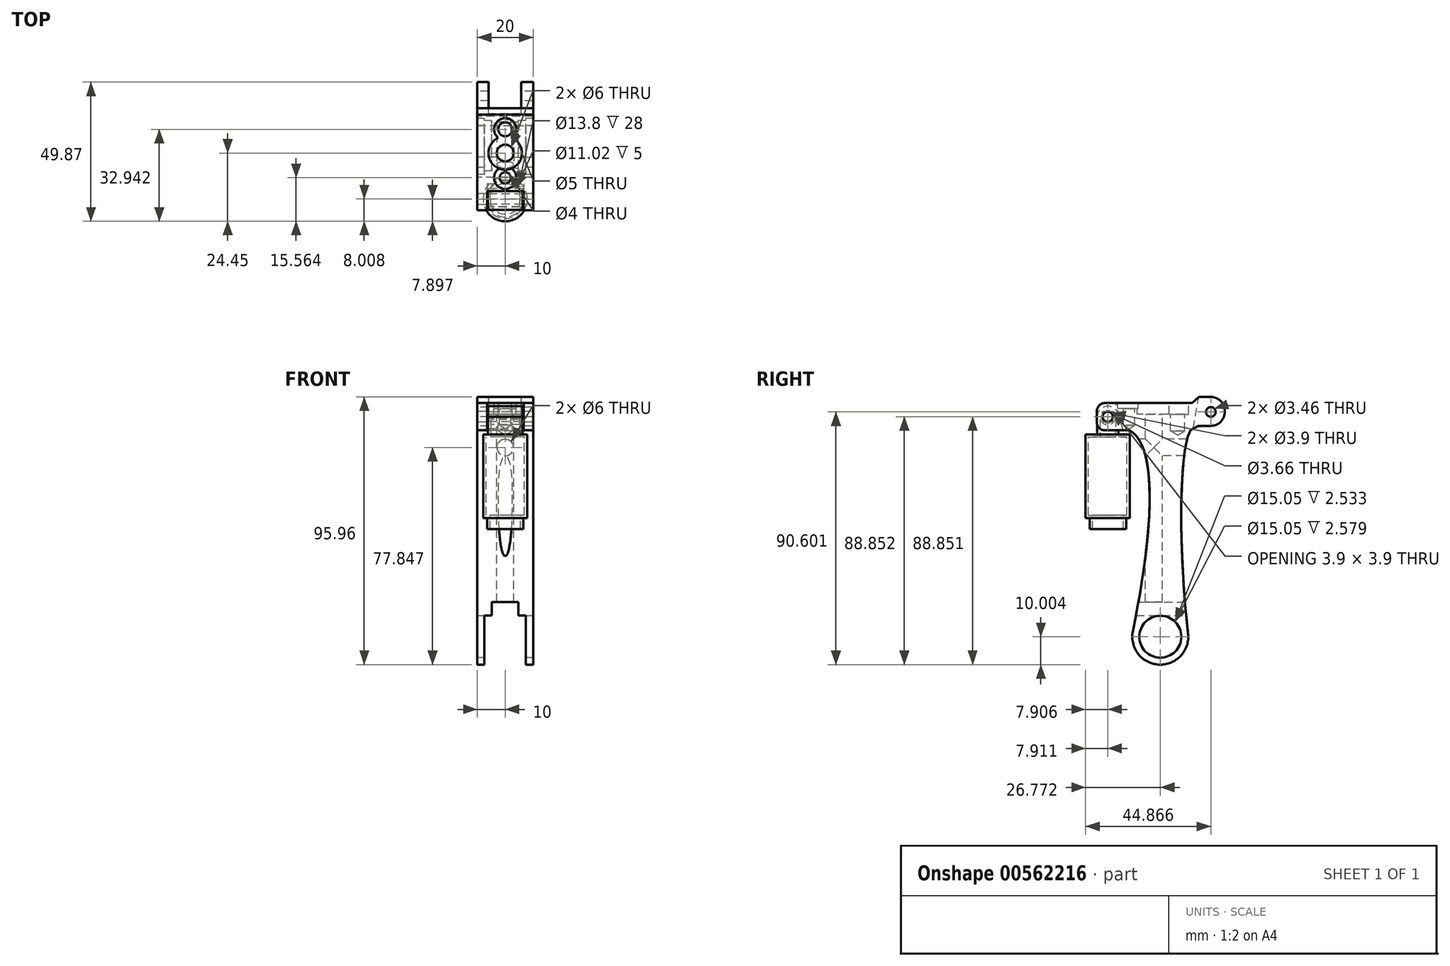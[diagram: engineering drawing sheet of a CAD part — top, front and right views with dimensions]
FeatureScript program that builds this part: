
annotation { "Feature Type Name" : "Feature", "Feature Type Description" : "" }
export const myFeature = defineFeature(function(context is Context, id is Id, definition is map)
    precondition{}
    {
        {
            var Q0;
            Q0=qCreatedBy(makeId("Right.planeOp"),FACE);
            var sketch = newSketch(context, id + "F0", { "sketchPlane" : qUnion([Q0])});
            skLineSegment(sketch, "E0", {"start": v(-11.53, -4.6) * mm, "end": v(-15.88, -4.6) * mm});
            skLineSegment(sketch, "E1", {"start": v(-15.88, -4.6) * mm, "end": v(-18.18, -6.8) * mm});
            skLineSegment(sketch, "E2", {"start": v(-18.18, -6.8) * mm, "end": v(-49.43, -6.8) * mm});
            skLineSegment(sketch, "E3", {"start": v(-52.43, -9.8) * mm, "end": v(-52.43, -13.6) * mm});
            skLineSegment(sketch, "E4", {"start": v(-49.43, -16.6) * mm, "end": v(-40.63, -16.6) * mm});
            skLineSegment(sketch, "E5", {"start": v(-6.53, -9.6) * mm, "end": v(-6.53, -9.97) * mm});
            skLineSegment(sketch, "E6", {"start": v(-11.53, -14.97) * mm, "end": v(-16.03, -14.97) * mm});
            skLineSegment(sketch, "E7", {"start": v(-16.03, -14.97) * mm, "end": v(-18.84, -16.6) * mm});
            skFitSpline(sketch, "E8", {"points": [v(-18.84, -16.6) * mm, v(-18.36, -99.99) * mm], "startDerivative": vector(-12.08, -19.93) * mm, "endDerivative": vector(16.3, -116.19) * mm});
            skFitSpline(sketch, "E9", {"points": [v(-40.63, -16.6) * mm, v(-42.25, -101.24) * mm], "startDerivative": vector(34.93, -19.93) * mm, "endDerivative": vector(-27.8, -119.95) * mm});
            skArc(sketch, "E10.filletArc", {"start": v(-6.53, -9.6) * mm, "mid": v(-8, -6.07) * mm, "end": v(-11.53, -4.6) * mm});
            skArc(sketch, "E11.filletArc", {"start": v(-11.53, -14.97) * mm, "mid": v(-8, -13.5) * mm, "end": v(-6.53, -9.97) * mm});
            skArc(sketch, "E12.filletArc", {"start": v(-49.43, -6.8) * mm, "mid": v(-51.55, -7.67) * mm, "end": v(-52.43, -9.8) * mm});
            skPoint(sketch, "E13.center.orphan", {"position": v(-30.3, -100.61) * mm});
            skLineSegment(sketch, "E14", {"start": v(-29.1, -100.55) * mm, "end": v(-29.16, -100.55) * mm});
            skArc(sketch, "E15.filletArc", {"start": v(-29.1, -100.55) * mm, "mid": v(-22, -97.03) * mm, "end": v(-19.7, -89.45) * mm});
            skArc(sketch, "E16.filletArc", {"start": v(-39.48, -88.56) * mm, "mid": v(-37.26, -97.1) * mm, "end": v(-29.16, -100.55) * mm});
            skArc(sketch, "E17.filletArc", {"start": v(-52.43, -13.6) * mm, "mid": v(-51.55, -15.72) * mm, "end": v(-49.43, -16.6) * mm});
            skCircle(sketch, "E18", {"center": v(-29.63, -90.57) * mm, "radius": 7.53 * mm});
            skCircle(sketch, "E19", {"center": v(-48.5, -11.72) * mm, "radius": 1.95 * mm});
            skCircle(sketch, "E20", {"center": v(-11.53, -9.97) * mm, "radius": 1.73 * mm});
            skSolve(sketch);
        }
        {
            var Q0;
            Q0 = qSketchRegion(id + "F0", true);
            extrude(context, id + "F1", {"entities" : qUnion([Q0]), "endBound" : BoundingType.SYMMETRIC, "depth" : 20 * mm, "offsetDistance" : 25 * mm});
        }
        {
            var Q0;
            Q0=makeQuery(id+"F1.opExtrude","SWEPT_FACE",FACE,{"disambiguationData":[OSD([sQuery(id+"F0.wireOp",EDGE,"E2")])]});
            var sketch = newSketch(context, id + "F2", { "sketchPlane" : qUnion([Q0])});
            skPoint(sketch, "E21", {"position": v(0, -31.95) * mm});
            skPoint(sketch, "E22", {"position": v(0, -23.46) * mm});
            skPoint(sketch, "E22.positionSnap0", {"position": v(0, -18.18) * mm});
            skPoint(sketch, "E23", {"position": v(0, -40.84) * mm});
            skSolve(sketch);
        }
        {
            var Q0;
            Q0=sQuery(id+"F2.wireOp",VERTEX,"E21");
            var Q1;
            Q1=makeQuery(id+"F1.opExtrude","SWEPT_BODY",BODY,{"disambiguationData":[OSD([sQuery(id+"F0.wireOp",EDGE,"E0"),sQuery(id+"F0.wireOp",EDGE,"E1"),sQuery(id+"F0.wireOp",EDGE,"E2"),sQuery(id+"F0.wireOp",EDGE,"E3"),sQuery(id+"F0.wireOp",EDGE,"E4"),sQuery(id+"F0.wireOp",EDGE,"E5"),sQuery(id+"F0.wireOp",EDGE,"E6"),sQuery(id+"F0.wireOp",EDGE,"E7"),sQuery(id+"F0.wireOp",EDGE,"E8"),sQuery(id+"F0.wireOp",EDGE,"E9"),sQuery(id+"F0.wireOp",EDGE,"E10.filletArc"),sQuery(id+"F0.wireOp",EDGE,"E11.filletArc"),sQuery(id+"F0.wireOp",EDGE,"E12.filletArc"),sQuery(id+"F0.wireOp",EDGE,"E14"),sQuery(id+"F0.wireOp",EDGE,"E15.filletArc"),sQuery(id+"F0.wireOp",EDGE,"E16.filletArc"),sQuery(id+"F0.wireOp",EDGE,"E17.filletArc"),sQuery(id+"F0.wireOp",EDGE,"E18"),sQuery(id+"F0.wireOp",EDGE,"E19"),sQuery(id+"F0.wireOp",EDGE,"E20")])]});
            hole(context, id + "F3", {"style" : HoleStyle.C_BORE, "endStyle" : HoleEndStyle.BLIND, "holeDiameter" : 6 * mm, "cBoreDiameter" : 12 * mm, "cBoreDepth" : 4 * mm, "majorDiameter" : 5 * mm, "holeDepth" : 80 * mm, "isTappedThrough" : true, "tappedDepth" : 12 * mm, "tapClearance" : 3, "startFromSketch" : true, "locations" : qUnion([Q0]), "scope" : qUnion([Q1])});
        }
        {
            var Q0;
            Q0=sQuery(id+"F2.wireOp",VERTEX,"E22");
            var Q1;
            Q1=makeQuery(id+"F1.opExtrude","SWEPT_BODY",BODY,{"disambiguationData":[OSD([sQuery(id+"F0.wireOp",EDGE,"E0"),sQuery(id+"F0.wireOp",EDGE,"E1"),sQuery(id+"F0.wireOp",EDGE,"E2"),sQuery(id+"F0.wireOp",EDGE,"E3"),sQuery(id+"F0.wireOp",EDGE,"E4"),sQuery(id+"F0.wireOp",EDGE,"E5"),sQuery(id+"F0.wireOp",EDGE,"E6"),sQuery(id+"F0.wireOp",EDGE,"E7"),sQuery(id+"F0.wireOp",EDGE,"E8"),sQuery(id+"F0.wireOp",EDGE,"E9"),sQuery(id+"F0.wireOp",EDGE,"E10.filletArc"),sQuery(id+"F0.wireOp",EDGE,"E11.filletArc"),sQuery(id+"F0.wireOp",EDGE,"E12.filletArc"),sQuery(id+"F0.wireOp",EDGE,"E14"),sQuery(id+"F0.wireOp",EDGE,"E15.filletArc"),sQuery(id+"F0.wireOp",EDGE,"E16.filletArc"),sQuery(id+"F0.wireOp",EDGE,"E17.filletArc"),sQuery(id+"F0.wireOp",EDGE,"E18"),sQuery(id+"F0.wireOp",EDGE,"E19"),sQuery(id+"F0.wireOp",EDGE,"E20")])]});
            hole(context, id + "F4", {"style" : HoleStyle.C_BORE, "endStyle" : HoleEndStyle.BLIND, "holeDiameter" : 5 * mm, "cBoreDiameter" : 8 * mm, "cBoreDepth" : 4 * mm, "majorDiameter" : 5 * mm, "holeDepth" : 10 * mm, "isTappedThrough" : true, "tappedDepth" : 12 * mm, "tapClearance" : 3, "startFromSketch" : true, "locations" : qUnion([Q0]), "scope" : qUnion([Q1])});
        }
        {
            var Q0;
            Q0=sQuery(id+"F2.wireOp",VERTEX,"E23");
            var Q1;
            Q1=makeQuery(id+"F1.opExtrude","SWEPT_BODY",BODY,{"disambiguationData":[OSD([sQuery(id+"F0.wireOp",EDGE,"E0"),sQuery(id+"F0.wireOp",EDGE,"E1"),sQuery(id+"F0.wireOp",EDGE,"E2"),sQuery(id+"F0.wireOp",EDGE,"E3"),sQuery(id+"F0.wireOp",EDGE,"E4"),sQuery(id+"F0.wireOp",EDGE,"E5"),sQuery(id+"F0.wireOp",EDGE,"E6"),sQuery(id+"F0.wireOp",EDGE,"E7"),sQuery(id+"F0.wireOp",EDGE,"E8"),sQuery(id+"F0.wireOp",EDGE,"E9"),sQuery(id+"F0.wireOp",EDGE,"E10.filletArc"),sQuery(id+"F0.wireOp",EDGE,"E11.filletArc"),sQuery(id+"F0.wireOp",EDGE,"E12.filletArc"),sQuery(id+"F0.wireOp",EDGE,"E14"),sQuery(id+"F0.wireOp",EDGE,"E15.filletArc"),sQuery(id+"F0.wireOp",EDGE,"E16.filletArc"),sQuery(id+"F0.wireOp",EDGE,"E17.filletArc"),sQuery(id+"F0.wireOp",EDGE,"E18"),sQuery(id+"F0.wireOp",EDGE,"E19"),sQuery(id+"F0.wireOp",EDGE,"E20")])]});
            hole(context, id + "F5", {"style" : HoleStyle.C_BORE, "endStyle" : HoleEndStyle.BLIND, "holeDiameter" : 4 * mm, "cBoreDiameter" : 8 * mm, "cBoreDepth" : 2 * mm, "majorDiameter" : 5 * mm, "holeDepth" : 8 * mm, "isTappedThrough" : true, "tappedDepth" : 12 * mm, "tapClearance" : 3, "startFromSketch" : true, "locations" : qUnion([Q0]), "scope" : qUnion([Q1])});
        }
        {
            var Q0;
            Q0=makeQuery(id+"F1.opExtrude","SWEPT_FACE",FACE,{"disambiguationData":[OSD([sQuery(id+"F0.wireOp",EDGE,"E3")])]});
            var sketch = newSketch(context, id + "F6", { "sketchPlane" : qUnion([Q0])});
            skPoint(sketch, "E24", {"position": v(0, -22.72) * mm});
            skPoint(sketch, "E25", {"position": v(0, -71.93) * mm});
            skSolve(sketch);
        }
        {
            var Q0;
            Q0=sQuery(id+"F6.wireOp",VERTEX,"E24");
            var Q1;
            Q1=makeQuery(id+"F1.opExtrude","SWEPT_BODY",BODY,{"disambiguationData":[OSD([sQuery(id+"F0.wireOp",EDGE,"E0"),sQuery(id+"F0.wireOp",EDGE,"E1"),sQuery(id+"F0.wireOp",EDGE,"E2"),sQuery(id+"F0.wireOp",EDGE,"E3"),sQuery(id+"F0.wireOp",EDGE,"E4"),sQuery(id+"F0.wireOp",EDGE,"E5"),sQuery(id+"F0.wireOp",EDGE,"E6"),sQuery(id+"F0.wireOp",EDGE,"E7"),sQuery(id+"F0.wireOp",EDGE,"E8"),sQuery(id+"F0.wireOp",EDGE,"E9"),sQuery(id+"F0.wireOp",EDGE,"E10.filletArc"),sQuery(id+"F0.wireOp",EDGE,"E11.filletArc"),sQuery(id+"F0.wireOp",EDGE,"E12.filletArc"),sQuery(id+"F0.wireOp",EDGE,"E14"),sQuery(id+"F0.wireOp",EDGE,"E15.filletArc"),sQuery(id+"F0.wireOp",EDGE,"E16.filletArc"),sQuery(id+"F0.wireOp",EDGE,"E17.filletArc"),sQuery(id+"F0.wireOp",EDGE,"E18"),sQuery(id+"F0.wireOp",EDGE,"E19"),sQuery(id+"F0.wireOp",EDGE,"E20")])]});
            hole(context, id + "F7", {"style" : HoleStyle.SIMPLE, "endStyle" : HoleEndStyle.BLIND, "holeDiameter" : 6 * mm, "majorDiameter" : 5 * mm, "holeDepth" : 40 * mm, "isTappedThrough" : true, "tappedDepth" : 12 * mm, "tapClearance" : 3, "startFromSketch" : true, "locations" : qUnion([Q0]), "scope" : qUnion([Q1])});
        }
        {
            var Q0;
            Q0=qCreatedBy(makeId("Front.planeOp"),FACE);
            var sketch = newSketch(context, id + "F8", { "sketchPlane" : qUnion([Q0])});
            skLineSegment(sketch, "E26.bottom", {"start": v(-7.47, -82.93) * mm, "end": v(7.42, -82.93) * mm});
            skLineSegment(sketch, "E26.top", {"start": v(-7.47, -100.7) * mm, "end": v(7.42, -100.7) * mm});
            skLineSegment(sketch, "E26.left", {"start": v(-7.47, -82.93) * mm, "end": v(-7.47, -100.7) * mm});
            skLineSegment(sketch, "E26.right", {"start": v(7.42, -82.93) * mm, "end": v(7.42, -100.7) * mm});
            skSolve(sketch);
        }
        {
            var Q0;
            Q0=makeQuery(id+"F8.imprint","IMPRINT",FACE,{"disambiguationData":[TD([[makeQuery(id+"F8.imprint","IMPRINT",EDGE,{"derivedFrom":sQuery(id+"F8.wireOp",EDGE,"E26.bottom")}),-1.0]])]});
            extrude(context, id + "F9", {"entities" : qUnion([Q0]), "endBound" : BoundingType.THROUGH_ALL, "depth" : 25 * mm, "offsetDistance" : 25 * mm});
        }
        {
            var Q0;
            Q0=makeQuery(id+"F9.opExtrude","SWEPT_BODY",BODY,{"disambiguationData":[OSD([sQuery(id+"F8.wireOp",EDGE,"E26.bottom"),sQuery(id+"F8.wireOp",EDGE,"E26.top"),sQuery(id+"F8.wireOp",EDGE,"E26.left"),sQuery(id+"F8.wireOp",EDGE,"E26.right")])]});
            var Q1;
            Q1=makeQuery(id+"F1.opExtrude","SWEPT_BODY",BODY,{"disambiguationData":[OSD([sQuery(id+"F0.wireOp",EDGE,"E0"),sQuery(id+"F0.wireOp",EDGE,"E1"),sQuery(id+"F0.wireOp",EDGE,"E2"),sQuery(id+"F0.wireOp",EDGE,"E3"),sQuery(id+"F0.wireOp",EDGE,"E4"),sQuery(id+"F0.wireOp",EDGE,"E5"),sQuery(id+"F0.wireOp",EDGE,"E6"),sQuery(id+"F0.wireOp",EDGE,"E7"),sQuery(id+"F0.wireOp",EDGE,"E8"),sQuery(id+"F0.wireOp",EDGE,"E9"),sQuery(id+"F0.wireOp",EDGE,"E10.filletArc"),sQuery(id+"F0.wireOp",EDGE,"E11.filletArc"),sQuery(id+"F0.wireOp",EDGE,"E12.filletArc"),sQuery(id+"F0.wireOp",EDGE,"E14"),sQuery(id+"F0.wireOp",EDGE,"E15.filletArc"),sQuery(id+"F0.wireOp",EDGE,"E16.filletArc"),sQuery(id+"F0.wireOp",EDGE,"E17.filletArc"),sQuery(id+"F0.wireOp",EDGE,"E18"),sQuery(id+"F0.wireOp",EDGE,"E19"),sQuery(id+"F0.wireOp",EDGE,"E20")])]});
            booleanBodies(context, id + "F10", {"operationType" : BooleanOperationType.SUBTRACTION, "tools" : qUnion([Q0]), "targets" : qUnion([Q1])});
        }
        {
            var Q0;
            Q0=qCreatedBy(makeId("Top.planeOp"),FACE);
            var sketch = newSketch(context, id + "F11", { "sketchPlane" : qUnion([Q0])});
            skLineSegment(sketch, "E27.bottom", {"start": v(-6.5, -47.75) * mm, "end": v(6.55, -47.75) * mm});
            skLineSegment(sketch, "E27.top", {"start": v(-6.5, -57.6) * mm, "end": v(6.55, -57.6) * mm});
            skLineSegment(sketch, "E27.left", {"start": v(-6.5, -47.75) * mm, "end": v(-6.5, -57.6) * mm});
            skLineSegment(sketch, "E27.right", {"start": v(6.55, -47.75) * mm, "end": v(6.55, -57.6) * mm});
            skSolve(sketch);
        }
        {
            var Q0;
            Q0 = qSketchRegion(id + "F11", true);
            extrude(context, id + "F12", {"entities" : qUnion([Q0]), "oppositeDirection" : true, "depth" : 25 * mm, "offsetDistance" : 25 * mm});
        }
        {
            var Q0;
            Q0=makeQuery(id+"F12.opExtrude","SWEPT_BODY",BODY,{"disambiguationData":[OSD([sQuery(id+"F11.wireOp",EDGE,"E27.bottom"),sQuery(id+"F11.wireOp",EDGE,"E27.top"),sQuery(id+"F11.wireOp",EDGE,"E27.left"),sQuery(id+"F11.wireOp",EDGE,"E27.right")])]});
            var Q1;
            Q1=makeQuery(id+"F12.opExtrude","CAP_EDGE",EDGE,{"disambiguationData":[OSD([sQuery(id+"F11.wireOp",EDGE,"E27.top")])],"isStart":true});
            transform(context, id + "F13", {"entities" : qUnion([Q0]), "transformType" : TransformType.ROTATION, "transformAxis" : qUnion([Q1]), "angle" : 15 * degree, "makeCopy" : false});
        }
        {
            var Q0;
            Q0=makeQuery(id+"F12.opExtrude","SWEPT_BODY",BODY,{"disambiguationData":[OSD([sQuery(id+"F11.wireOp",EDGE,"E27.bottom"),sQuery(id+"F11.wireOp",EDGE,"E27.top"),sQuery(id+"F11.wireOp",EDGE,"E27.left"),sQuery(id+"F11.wireOp",EDGE,"E27.right")])]});
            var Q1;
            Q1=makeQuery(id+"F1.opExtrude","SWEPT_BODY",BODY,{"disambiguationData":[OSD([sQuery(id+"F0.wireOp",EDGE,"E0"),sQuery(id+"F0.wireOp",EDGE,"E1"),sQuery(id+"F0.wireOp",EDGE,"E2"),sQuery(id+"F0.wireOp",EDGE,"E3"),sQuery(id+"F0.wireOp",EDGE,"E4"),sQuery(id+"F0.wireOp",EDGE,"E5"),sQuery(id+"F0.wireOp",EDGE,"E6"),sQuery(id+"F0.wireOp",EDGE,"E7"),sQuery(id+"F0.wireOp",EDGE,"E8"),sQuery(id+"F0.wireOp",EDGE,"E9"),sQuery(id+"F0.wireOp",EDGE,"E10.filletArc"),sQuery(id+"F0.wireOp",EDGE,"E11.filletArc"),sQuery(id+"F0.wireOp",EDGE,"E12.filletArc"),sQuery(id+"F0.wireOp",EDGE,"E14"),sQuery(id+"F0.wireOp",EDGE,"E15.filletArc"),sQuery(id+"F0.wireOp",EDGE,"E16.filletArc"),sQuery(id+"F0.wireOp",EDGE,"E17.filletArc"),sQuery(id+"F0.wireOp",EDGE,"E18"),sQuery(id+"F0.wireOp",EDGE,"E19"),sQuery(id+"F0.wireOp",EDGE,"E20")])]});
            booleanBodies(context, id + "F14", {"operationType" : BooleanOperationType.SUBTRACTION, "tools" : qUnion([Q0]), "targets" : qUnion([Q1])});
        }
        {
            var Q0;
            Q0=qCreatedBy(makeId("Top.planeOp"),FACE);
            var sketch = newSketch(context, id + "F15", { "sketchPlane" : qUnion([Q0])});
            skLineSegment(sketch, "E28.bottom", {"start": v(-4.83, -40.06) * mm, "end": v(4.68, -40.06) * mm});
            skLineSegment(sketch, "E28.top", {"start": v(-4.83, -19.56) * mm, "end": v(4.68, -19.56) * mm});
            skLineSegment(sketch, "E28.left", {"start": v(-4.83, -40.06) * mm, "end": v(-4.83, -19.56) * mm});
            skLineSegment(sketch, "E28.right", {"start": v(4.68, -40.06) * mm, "end": v(4.68, -19.56) * mm});
            skSolve(sketch);
        }
        {
            var Q0;
            Q0 = qSketchRegion(id + "F15", true);
            extrude(context, id + "F16", {"entities" : qUnion([Q0]), "oppositeDirection" : true, "depth" : 10 * mm, "offsetDistance" : 25 * mm});
        }
        {
            var Q0;
            Q0=makeQuery(id+"F16.opExtrude","SWEPT_BODY",BODY,{"disambiguationData":[OSD([sQuery(id+"F15.wireOp",EDGE,"E28.bottom"),sQuery(id+"F15.wireOp",EDGE,"E28.top"),sQuery(id+"F15.wireOp",EDGE,"E28.left"),sQuery(id+"F15.wireOp",EDGE,"E28.right")])]});
            transform(context, id + "F17", {"entities" : qUnion([Q0]), "transformType" : TransformType.TRANSLATION_3D, "dx" : 0 * mm, "dy" : 1.5 * mm, "dz" : -78.1 * mm, "makeCopy" : false});
        }
        {
            var Q0;
            Q0=makeQuery(id+"F16.opExtrude","SWEPT_BODY",BODY,{"disambiguationData":[OSD([sQuery(id+"F15.wireOp",EDGE,"E28.bottom"),sQuery(id+"F15.wireOp",EDGE,"E28.top"),sQuery(id+"F15.wireOp",EDGE,"E28.left"),sQuery(id+"F15.wireOp",EDGE,"E28.right")])]});
            var Q1;
            Q1=makeQuery(id+"F1.opExtrude","SWEPT_BODY",BODY,{"disambiguationData":[OSD([sQuery(id+"F0.wireOp",EDGE,"E0"),sQuery(id+"F0.wireOp",EDGE,"E1"),sQuery(id+"F0.wireOp",EDGE,"E2"),sQuery(id+"F0.wireOp",EDGE,"E3"),sQuery(id+"F0.wireOp",EDGE,"E4"),sQuery(id+"F0.wireOp",EDGE,"E5"),sQuery(id+"F0.wireOp",EDGE,"E6"),sQuery(id+"F0.wireOp",EDGE,"E7"),sQuery(id+"F0.wireOp",EDGE,"E8"),sQuery(id+"F0.wireOp",EDGE,"E9"),sQuery(id+"F0.wireOp",EDGE,"E10.filletArc"),sQuery(id+"F0.wireOp",EDGE,"E11.filletArc"),sQuery(id+"F0.wireOp",EDGE,"E12.filletArc"),sQuery(id+"F0.wireOp",EDGE,"E14"),sQuery(id+"F0.wireOp",EDGE,"E15.filletArc"),sQuery(id+"F0.wireOp",EDGE,"E16.filletArc"),sQuery(id+"F0.wireOp",EDGE,"E17.filletArc"),sQuery(id+"F0.wireOp",EDGE,"E18"),sQuery(id+"F0.wireOp",EDGE,"E19"),sQuery(id+"F0.wireOp",EDGE,"E20")])]});
            booleanBodies(context, id + "F18", {"operationType" : BooleanOperationType.SUBTRACTION, "tools" : qUnion([Q0]), "targets" : qUnion([Q1])});
        }
        {
            var Q0;
            Q0=qCreatedBy(makeId("Top.planeOp"),FACE);
            var sketch = newSketch(context, id + "F19", { "sketchPlane" : qUnion([Q0])});
            skLineSegment(sketch, "E29.bottom", {"start": v(-5.92, -4.62) * mm, "end": v(5.71, -4.62) * mm});
            skLineSegment(sketch, "E29.top", {"start": v(-5.92, -14.89) * mm, "end": v(5.71, -14.89) * mm});
            skLineSegment(sketch, "E29.left", {"start": v(-5.92, -4.62) * mm, "end": v(-5.92, -14.89) * mm});
            skLineSegment(sketch, "E29.right", {"start": v(5.71, -4.62) * mm, "end": v(5.71, -14.89) * mm});
            skSolve(sketch);
        }
        {
            var Q0;
            Q0=makeQuery(id+"F19.imprint","IMPRINT",FACE,{"disambiguationData":[TD([[makeQuery(id+"F19.imprint","IMPRINT",EDGE,{"derivedFrom":sQuery(id+"F19.wireOp",EDGE,"E29.bottom")}),-1.0]])]});
            extrude(context, id + "F20", {"entities" : qUnion([Q0]), "oppositeDirection" : true, "depth" : 25 * mm, "offsetDistance" : 25 * mm});
        }
        {
            var Q0;
            Q0=makeQuery(id+"F20.opExtrude","SWEPT_BODY",BODY,{"disambiguationData":[OSD([sQuery(id+"F19.wireOp",EDGE,"E29.bottom"),sQuery(id+"F19.wireOp",EDGE,"E29.top"),sQuery(id+"F19.wireOp",EDGE,"E29.left"),sQuery(id+"F19.wireOp",EDGE,"E29.right")])]});
            var Q1;
            Q1=makeQuery(id+"F20.opExtrude","CAP_EDGE",EDGE,{"disambiguationData":[OSD([sQuery(id+"F19.wireOp",EDGE,"E29.bottom")])],"isStart":true});
            transform(context, id + "F21", {"entities" : qUnion([Q0]), "transformType" : TransformType.ROTATION, "transformAxis" : qUnion([Q1]), "angle" : 10 * degree, "oppositeDirection" : true, "makeCopy" : false});
        }
        {
            var Q0;
            Q0=makeQuery(id+"F20.opExtrude","SWEPT_BODY",BODY,{"disambiguationData":[OSD([sQuery(id+"F19.wireOp",EDGE,"E29.bottom"),sQuery(id+"F19.wireOp",EDGE,"E29.top"),sQuery(id+"F19.wireOp",EDGE,"E29.left"),sQuery(id+"F19.wireOp",EDGE,"E29.right")])]});
            var Q1;
            Q1=makeQuery(id+"F1.opExtrude","SWEPT_BODY",BODY,{"disambiguationData":[OSD([sQuery(id+"F0.wireOp",EDGE,"E0"),sQuery(id+"F0.wireOp",EDGE,"E1"),sQuery(id+"F0.wireOp",EDGE,"E2"),sQuery(id+"F0.wireOp",EDGE,"E3"),sQuery(id+"F0.wireOp",EDGE,"E4"),sQuery(id+"F0.wireOp",EDGE,"E5"),sQuery(id+"F0.wireOp",EDGE,"E6"),sQuery(id+"F0.wireOp",EDGE,"E7"),sQuery(id+"F0.wireOp",EDGE,"E8"),sQuery(id+"F0.wireOp",EDGE,"E9"),sQuery(id+"F0.wireOp",EDGE,"E10.filletArc"),sQuery(id+"F0.wireOp",EDGE,"E11.filletArc"),sQuery(id+"F0.wireOp",EDGE,"E12.filletArc"),sQuery(id+"F0.wireOp",EDGE,"E14"),sQuery(id+"F0.wireOp",EDGE,"E15.filletArc"),sQuery(id+"F0.wireOp",EDGE,"E16.filletArc"),sQuery(id+"F0.wireOp",EDGE,"E17.filletArc"),sQuery(id+"F0.wireOp",EDGE,"E18"),sQuery(id+"F0.wireOp",EDGE,"E19"),sQuery(id+"F0.wireOp",EDGE,"E20")])]});
            booleanBodies(context, id + "F22", {"operationType" : BooleanOperationType.SUBTRACTION, "tools" : qUnion([Q0]), "targets" : qUnion([Q1])});
        }
        {
            var Q0;
            Q0=qCreatedBy(makeId("Top.planeOp"),FACE);
            var sketch = newSketch(context, id + "F23", { "sketchPlane" : qUnion([Q0])});
            skCircle(sketch, "E30", {"center": v(0, -47.5) * mm, "radius": 7.9 * mm});
            skSolve(sketch);
        }
        {
            var Q0;
            Q0=makeQuery(id+"F23.imprint","IMPRINT",FACE,{"disambiguationData":[TD([[makeQuery(id+"F23.imprint","IMPRINT",EDGE,{"derivedFrom":sQuery(id+"F23.wireOp",EDGE,"E30")}),1.0]])]});
            extrude(context, id + "F24", {"entities" : qUnion([Q0]), "oppositeDirection" : true, "depth" : 30 * mm, "offsetDistance" : 25 * mm});
        }
        {
            var Q0;
            Q0=makeQuery(id+"F24.opExtrude","SWEPT_BODY",BODY,{"disambiguationData":[OSD([sQuery(id+"F23.wireOp",EDGE,"E30")])]});
            transform(context, id + "F25", {"entities" : qUnion([Q0]), "transformType" : TransformType.TRANSLATION_3D, "dx" : 0 * mm, "dy" : -1 * mm, "dz" : -18 * mm, "makeCopy" : false});
        }
        {
            var Q0;
            Q0=qCreatedBy(makeId("Right.planeOp"),FACE);
            var sketch = newSketch(context, id + "F26", { "sketchPlane" : qUnion([Q0])});
            skArc(sketch, "E31", {"start": v(-44.7, -11.72) * mm, "mid": v(-48.49, -7.93) * mm, "end": v(-52.27, -11.72) * mm});
            skCircle(sketch, "E32", {"center": v(-48.49, -11.72) * mm, "radius": 1.83 * mm});
            skLineSegment(sketch, "E33.top", {"start": v(-44.7, -18.1) * mm, "end": v(-52.3, -18.1) * mm});
            skLineSegment(sketch, "E33.left", {"start": v(-44.7, -11.72) * mm, "end": v(-44.7, -18.1) * mm});
            skLineSegment(sketch, "E33.right", {"start": v(-52.3, -11.72) * mm, "end": v(-52.3, -18.1) * mm});
            skLineSegment(sketch, "E34.trimOffspring", {"start": v(-52.27, -11.72) * mm, "end": v(-52.3, -11.72) * mm});
            skSolve(sketch);
        }
        {
            var Q0;
            Q0 = qSketchRegion(id + "F26", true);
            extrude(context, id + "F27", {"entities" : qUnion([Q0]), "operationType" : NewBodyOperationType.ADD, "endBound" : BoundingType.SYMMETRIC, "depth" : 12.5 * mm, "offsetDistance" : 25 * mm});
        }
        {
            var Q0;
            Q0=qCreatedBy(makeId("Top.planeOp"),FACE);
            cPlane(context, id + "F28", {"entities" : qUnion([Q0]), "cplaneType" : CPlaneType.OFFSET, "offset" : 48 * mm, "oppositeDirection" : true, "width" : 150 * mm, "height" : 150 * mm});
        }
        {
            var Q0;
            Q0=qCreatedBy(id+"F28.planeOp",FACE);
            var sketch = newSketch(context, id + "F29", { "sketchPlane" : qUnion([Q0])});
            skCircle(sketch, "E35", {"center": v(0, -48.4) * mm, "radius": 6.51 * mm});
            skSolve(sketch);
        }
        {
            var Q0;
            Q0=makeQuery(id+"F29.imprint","IMPRINT",FACE,{"disambiguationData":[TD([[makeQuery(id+"F29.imprint","IMPRINT",EDGE,{"derivedFrom":sQuery(id+"F29.wireOp",EDGE,"E35")}),1.0]])]});
            extrude(context, id + "F30", {"entities" : qUnion([Q0]), "operationType" : NewBodyOperationType.ADD, "oppositeDirection" : true, "depth" : 4 * mm, "offsetDistance" : 25 * mm});
        }
        {
            var Q0;
            Q0=makeQuery(id+"F30.opExtrude","CAP_FACE",FACE,{"disambiguationData":[OSD([sQuery(id+"F29.wireOp",EDGE,"E35")])],"isStart":false});
            shell(context, id + "F31", {"entities" : qUnion([Q0]), "thickness" : 1 * mm});
        }
    });
